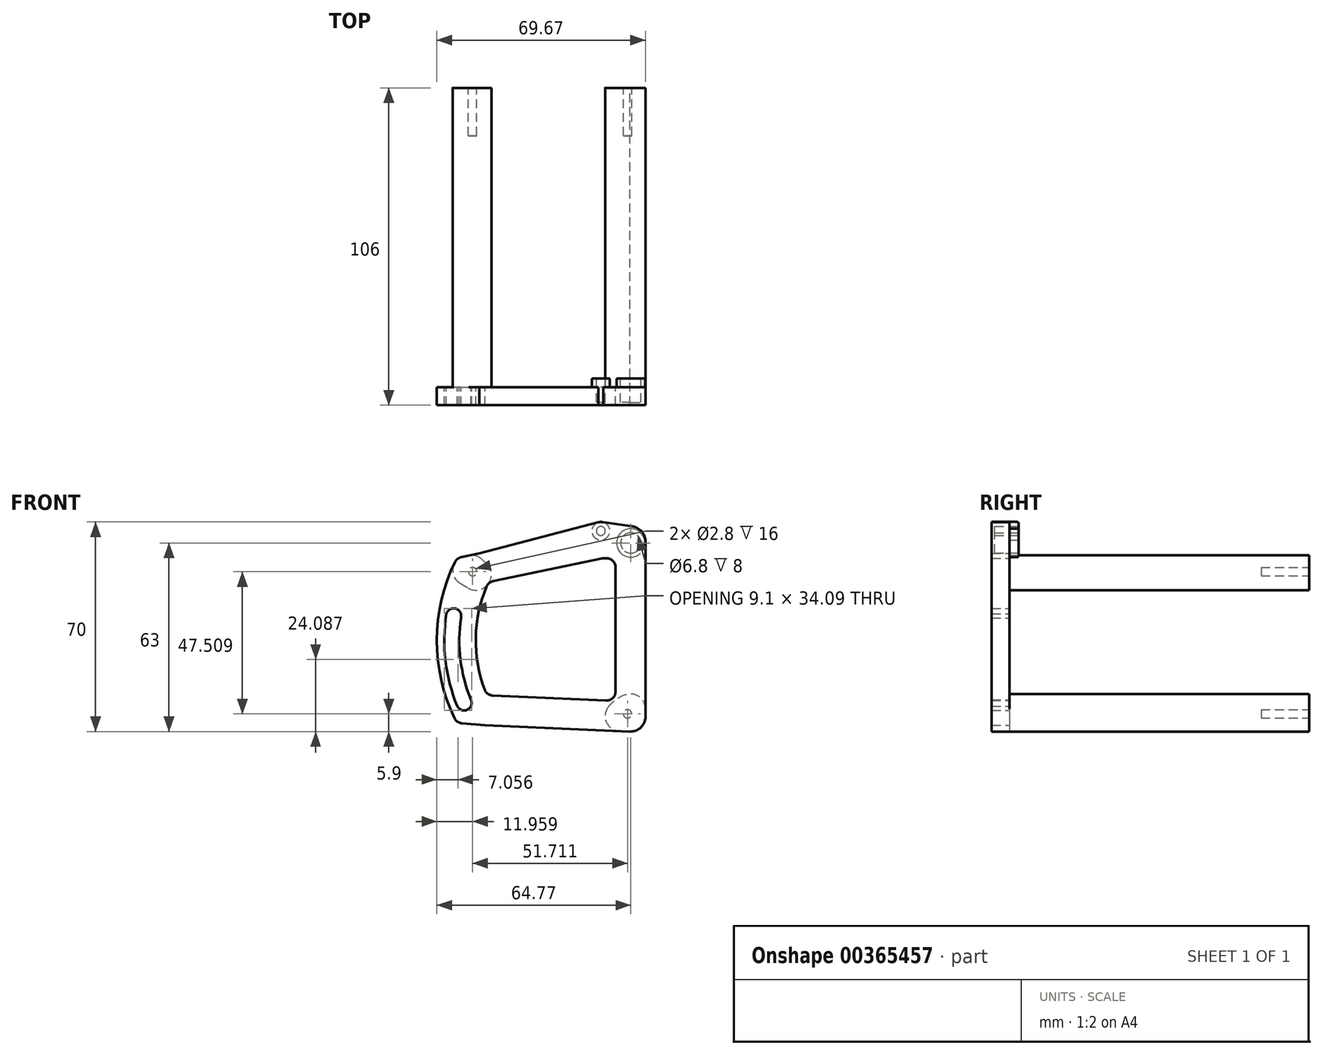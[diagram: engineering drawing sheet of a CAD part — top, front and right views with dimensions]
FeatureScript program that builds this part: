
annotation { "Feature Type Name" : "Feature", "Feature Type Description" : "" }
export const myFeature = defineFeature(function(context is Context, id is Id, definition is map)
    precondition{}
    {
        {
            var Q0;
            Q0=qCreatedBy(makeId("Front.planeOp"),FACE);
            var sketch = newSketch(context, id + "F0", { "sketchPlane" : qUnion([Q0])});
            skLineSegment(sketch, "E0", {"start": v(0, 0) * mm, "end": v(0, 70) * mm});
            skLineSegment(sketch, "E1", {"start": v(-63, 5) * mm, "end": v(0, 0) * mm});
            skLineSegment(sketch, "E2", {"start": v(-63, 60) * mm, "end": v(-39, 65) * mm});
            skArc(sketch, "E3", {"start": v(-63, 60) * mm, "mid": v(-69.67, 32.5) * mm, "end": v(-63, 5) * mm});
            skLineSegment(sketch, "E4.0", {"start": v(-10, 60) * mm, "end": v(-13.97, 60) * mm});
            skLineSegment(sketch, "E4.1", {"start": v(-52.44, 51.98) * mm, "end": v(-13.97, 60) * mm});
            skLineSegment(sketch, "E4.2", {"start": v(-10, 12.33) * mm, "end": v(-10, 60) * mm});
            skCircle(sketch, "E5", {"center": v(-4.9, 65.1) * mm, "radius": 3.4 * mm});
            skPoint(sketch, "E6.endSnap0", {"position": v(-59.67, 32.9) * mm});
            skArc(sketch, "E7.0", {"start": v(-52.44, 51.98) * mm, "mid": v(-56.67, 33.17) * mm, "end": v(-52.98, 14.24) * mm});
            skArc(sketch, "E8.0.left", {"start": v(-61.63, 40.03) * mm, "mid": v(-61.79, 26.15) * mm, "end": v(-58.3, 12.71) * mm});
            skArc(sketch, "E8.0.right", {"start": v(-66.48, 41.42) * mm, "mid": v(-66.78, 25.74) * mm, "end": v(-62.83, 10.57) * mm});
            skArc(sketch, "E9", {"start": v(-62.83, 10.57) * mm, "mid": v(-59.5, 9.38) * mm, "end": v(-58.3, 12.71) * mm});
            skPoint(sketch, "E10.endSnap0", {"position": v(-67.17, 32.96) * mm});
            skArc(sketch, "E11", {"start": v(-61.63, 40.03) * mm, "mid": v(-63.36, 43.15) * mm, "end": v(-66.48, 41.42) * mm});
            skPoint(sketch, "E10.end.orphan", {"position": v(-67.17, 32.92) * mm});
            skLineSegment(sketch, "E12", {"start": v(-4.9, 65.1) * mm, "end": v(-14.9, 65.1) * mm});
            skLineSegment(sketch, "E13", {"start": v(-14.9, 65.1) * mm, "end": v(-14.9, 69.1) * mm});
            skCircle(sketch, "E14", {"center": v(-14.9, 69.1) * mm, "radius": 1.5 * mm});
            skArc(sketch, "E15", {"start": v(-14.06, 71.98) * mm, "mid": v(-14.91, 72.1) * mm, "end": v(-15.76, 71.97) * mm});
            skLineSegment(sketch, "E16", {"start": v(0, 70) * mm, "end": v(-14.06, 71.98) * mm});
            skLineSegment(sketch, "E17", {"start": v(-39, 65) * mm, "end": v(-15.76, 71.97) * mm});
            skLineSegment(sketch, "E18", {"start": v(-4.9, 65.1) * mm, "end": v(5.1, 65.1) * mm});
            skLineSegment(sketch, "E19", {"start": v(5.1, 65.1) * mm, "end": v(5.1, 75.1) * mm});
            skLineSegment(sketch, "E20", {"start": v(5.1, 75.1) * mm, "end": v(5.1, 2.1) * mm});
            skLineSegment(sketch, "E21", {"start": v(-10, 12.33) * mm, "end": v(-52.98, 14.24) * mm});
            skSolve(sketch);
        }
        {
            var Q0;
            Q0 = qSketchRegion(id + "F0", true);
            extrude(context, id + "F1", {"entities" : qUnion([Q0]), "depth" : 6 * mm});
        }
        {
            var Q0;
            Q0=makeQuery(id+"F1.opExtrude","SWEPT_EDGE",EDGE,{"disambiguationData":[OSD([sQuery(id+"F0.wireOp",EDGE,"E1"),sQuery(id+"F0.wireOp",EDGE,"E3")])]});
            var Q1;
            Q1=makeQuery(id+"F1.opExtrude","SWEPT_EDGE",EDGE,{"disambiguationData":[OSD([sQuery(id+"F0.wireOp",EDGE,"E2"),sQuery(id+"F0.wireOp",EDGE,"E3")])]});
            var Q2;
            Q2=makeQuery(id+"F1.opExtrude","SWEPT_EDGE",EDGE,{"disambiguationData":[OSD([sQuery(id+"F0.wireOp",EDGE,"kmYFCEJS-3rxs-r7UX-FBYq-gBhfxVAc6up7"),sQuery(id+"F0.wireOp",EDGE,"E2")])]});
            var Q3;
            Q3=makeQuery(id+"F1.opExtrude","SWEPT_EDGE",EDGE,{"disambiguationData":[OSD([sQuery(id+"F0.wireOp",EDGE,"E4.3"),sQuery(id+"F0.wireOp",EDGE,"E7.0")])]});
            var Q4;
            Q4=makeQuery(id+"F1.opExtrude","SWEPT_EDGE",EDGE,{"disambiguationData":[OSD([sQuery(id+"F0.wireOp",EDGE,"E4.1"),sQuery(id+"F0.wireOp",EDGE,"E7.0")])]});
            var Q5;
            Q5=makeQuery(id+"F1.opExtrude","SWEPT_EDGE",EDGE,{"disambiguationData":[OSD([sQuery(id+"F0.wireOp",EDGE,"E4.0"),sQuery(id+"F0.wireOp",EDGE,"E4.2")])]});
            var Q6;
            Q6=makeQuery(id+"F1.opExtrude","SWEPT_EDGE",EDGE,{"disambiguationData":[OSD([sQuery(id+"F0.wireOp",EDGE,"E4.0"),sQuery(id+"F0.wireOp",EDGE,"E4.1")])]});
            var Q7;
            Q7=makeQuery(id+"F1.opExtrude","SWEPT_EDGE",EDGE,{"disambiguationData":[OSD([sQuery(id+"F0.wireOp",EDGE,"E4.2"),sQuery(id+"F0.wireOp",EDGE,"E4.3")])]});
            fillet(context, id + "F2", {"entities" : qUnion([Q0, Q1, Q2, Q3, Q4, Q5, Q6, Q7]), "radius" : 3 * mm, "tangentPropagation" : true, "allowEdgeOverflow" : false});
        }
        {
            var Q0;
            Q0=makeQuery(id+"F1.opExtrude","CAP_FACE",FACE,{"disambiguationData":[OSD([sQuery(id+"F0.wireOp",EDGE,"E0"),sQuery(id+"F0.wireOp",EDGE,"kmYFCEJS-3rxs-r7UX-FBYq-gBhfxVAc6up7"),sQuery(id+"F0.wireOp",EDGE,"E1"),sQuery(id+"F0.wireOp",EDGE,"E2"),sQuery(id+"F0.wireOp",EDGE,"E3"),sQuery(id+"F0.wireOp",EDGE,"E4.0"),sQuery(id+"F0.wireOp",EDGE,"E4.1"),sQuery(id+"F0.wireOp",EDGE,"E4.2"),sQuery(id+"F0.wireOp",EDGE,"E4.3"),sQuery(id+"F0.wireOp",EDGE,"E5"),sQuery(id+"F0.wireOp",EDGE,"jneuIOKs-55e1-7TO2-QkRI-z34TiCrGb9SQ"),sQuery(id+"F0.wireOp",EDGE,"E7.0"),sQuery(id+"F0.wireOp",EDGE,"E8.0.left"),sQuery(id+"F0.wireOp",EDGE,"E8.0.right"),sQuery(id+"F0.wireOp",EDGE,"775hFTDc-WrRt-JcbV-c3o9-qAtFPoJClycm"),sQuery(id+"F0.wireOp",EDGE,"E9")])],"isStart":true});
            var sketch = newSketch(context, id + "F3", { "sketchPlane" : qUnion([Q0])});
            skLineSegment(sketch, "E22", {"start": v(3.24, 0.26) * mm, "end": v(14.95, 1.19) * mm});
            skLineSegment(sketch, "E23", {"start": v(0, 3.25) * mm, "end": v(0, 15) * mm});
            skLineSegment(sketch, "E24", {"start": v(0, 15) * mm, "end": v(10, 15) * mm});
            skLineSegment(sketch, "E25", {"start": v(14.95, 1.19) * mm, "end": v(14.95, 11.22) * mm});
            skLineSegment(sketch, "E26.0", {"start": v(-0.8, 9.97) * mm, "end": v(0, 10.03) * mm});
            skLineSegment(sketch, "E27.0", {"start": v(10, 0) * mm, "end": v(10, 0.8) * mm});
            skLineSegment(sketch, "E28", {"start": v(14.16, 11.16) * mm, "end": v(14.95, 11.22) * mm});
            skLineSegment(sketch, "E29.trimOffspring", {"start": v(10, 14.07) * mm, "end": v(10, 15) * mm});
            skLineSegment(sketch, "E30.trimOffspring", {"start": v(13.24, 11.08) * mm, "end": v(14.16, 11.16) * mm});
            skPoint(sketch, "E31.visualSharp", {"position": v(0, 0) * mm});
            skArc(sketch, "E31.filletArc", {"start": v(0, 3.25) * mm, "mid": v(0.96, 1.04) * mm, "end": v(3.24, 0.26) * mm});
            skPoint(sketch, "E32.visualSharp", {"position": v(10, 10.83) * mm});
            skArc(sketch, "E32.filletArc", {"start": v(10, 14.07) * mm, "mid": v(10.96, 11.87) * mm, "end": v(13.24, 11.08) * mm});
            skArc(sketch, "E33", {"start": v(65.72, 53.91) * mm, "mid": v(64.75, 56.31) * mm, "end": v(63.67, 58.67) * mm});
            skArc(sketch, "E34.0", {"start": v(54.33, 47.14) * mm, "mid": v(53.74, 48.84) * mm, "end": v(53.08, 50.51) * mm});
            skLineSegment(sketch, "E35", {"start": v(47.41, 53.03) * mm, "end": v(50.93, 52.3) * mm});
            skLineSegment(sketch, "E36", {"start": v(56.52, 61.35) * mm, "end": v(61.58, 60.3) * mm});
            skArc(sketch, "E37", {"start": v(63.67, 58.67) * mm, "mid": v(62.81, 59.72) * mm, "end": v(61.58, 60.3) * mm});
            skArc(sketch, "E38", {"start": v(53.08, 50.51) * mm, "mid": v(52.23, 51.67) * mm, "end": v(50.93, 52.3) * mm});
            skPoint(sketch, "E39.center.orphan", {"position": v(62.81, 59.72) * mm});
            skPoint(sketch, "E40.center.orphan", {"position": v(52.23, 51.67) * mm});
            skLineSegment(sketch, "E41", {"start": v(65.72, 53.91) * mm, "end": v(54.33, 47.14) * mm});
            skLineSegment(sketch, "E42", {"start": v(56.52, 61.35) * mm, "end": v(47.41, 53.03) * mm});
            skSolve(sketch);
        }
        {
            var Q0;
            Q0 = qSketchRegion(id + "F3", true);
            extrude(context, id + "F4", {"entities" : qUnion([Q0]), "operationType" : NewBodyOperationType.ADD, "depth" : 100 * mm});
        }
        {
            var Q0;
            Q0=makeQuery(id+"F4.opExtrude","SWEPT_EDGE",EDGE,{"disambiguationData":[OSD([sQuery(id+"F0.wireOp",EDGE,"E4.3"),sQuery(id+"F3.wireOp",EDGE,"E25"),sQuery(id+"F3.wireOp",EDGE,"E28")])]});
            var Q1;
            Q1=makeQuery(id+"F4.opExtrude","SWEPT_EDGE",EDGE,{"disambiguationData":[OSD([sQuery(id+"F0.wireOp",EDGE,"E4.2"),sQuery(id+"F3.wireOp",EDGE,"E24"),sQuery(id+"F3.wireOp",EDGE,"E29.trimOffspring")])]});
            fillet(context, id + "F5", {"entities" : qUnion([Q0, Q1]), "radius" : 12 * mm, "tangentPropagation" : true, "allowEdgeOverflow" : false});
        }
        {
            var Q0;
            Q0=makeQuery(id+"F4.opExtrude","SWEPT_EDGE",EDGE,{"disambiguationData":[OSD([sQuery(id+"F0.wireOp",EDGE,"E0"),sQuery(id+"F3.wireOp",EDGE,"E23"),sQuery(id+"F3.wireOp",EDGE,"E24")])]});
            var Q1;
            Q1=makeQuery(id+"F4.opExtrude","SWEPT_EDGE",EDGE,{"disambiguationData":[OSD([sQuery(id+"F0.wireOp",EDGE,"E1"),sQuery(id+"F3.wireOp",EDGE,"E22"),sQuery(id+"F3.wireOp",EDGE,"E25")])]});
            fillet(context, id + "F6", {"entities" : qUnion([Q0, Q1]), "radius" : 5 * mm, "tangentPropagation" : true, "allowEdgeOverflow" : false});
        }
        {
            var Q0;
            Q0=makeQuery(id+"F4.opExtrude","SWEPT_EDGE",EDGE,{"disambiguationData":[OSD([sQuery(id+"F0.wireOp",EDGE,"E7.0"),sQuery(id+"F3.wireOp",EDGE,"E34.0"),sQuery(id+"F3.wireOp",EDGE,"E41")])]});
            var Q1;
            Q1=makeQuery(id+"F4.opExtrude","SWEPT_EDGE",EDGE,{"disambiguationData":[OSD([sQuery(id+"F0.wireOp",EDGE,"E4.1"),sQuery(id+"F3.wireOp",EDGE,"E35"),sQuery(id+"F3.wireOp",EDGE,"E42")])]});
            var Q2;
            Q2=makeQuery(id+"F4.opExtrude","SWEPT_EDGE",EDGE,{"disambiguationData":[OSD([sQuery(id+"F0.wireOp",EDGE,"E2"),sQuery(id+"F3.wireOp",EDGE,"E36"),sQuery(id+"F3.wireOp",EDGE,"E42")])]});
            var Q3;
            Q3=makeQuery(id+"F4.opExtrude","SWEPT_EDGE",EDGE,{"disambiguationData":[OSD([sQuery(id+"F0.wireOp",EDGE,"E3"),sQuery(id+"F3.wireOp",EDGE,"E33"),sQuery(id+"F3.wireOp",EDGE,"E41")])]});
            fillet(context, id + "F7", {"entities" : qUnion([Q0, Q1, Q2, Q3]), "radius" : 5 * mm, "tangentPropagation" : true, "allowEdgeOverflow" : false});
        }
        {
            var Q0;
            {var subQ0=sQuery(id+"F0.wireOp",EDGE,"E2");var subQ1=sQuery(id+"F0.wireOp",EDGE,"kmYFCEJS-3rxs-r7UX-FBYq-gBhfxVAc6up7");var subQ2=sQuery(id+"F0.wireOp",EDGE,"E5");var subQ3=sQuery(id+"F0.wireOp",EDGE,"jneuIOKs-55e1-7TO2-QkRI-z34TiCrGb9SQ");var subQ4=sQuery(id+"F0.wireOp",EDGE,"E4.2");var subQ5=sQuery(id+"F0.wireOp",EDGE,"E4.1");var subQ6=sQuery(id+"F0.wireOp",EDGE,"E0");var subQ7=sQuery(id+"F0.wireOp",EDGE,"E4.0");Q0=makeQuery(id+"F4.boolean.opBoolean","SPLIT",FACE,{"disambiguationData":[TD([makeQuery(id+"F1.opExtrude","SWEPT_FACE",FACE,{"disambiguationData":[OSD([subQ6])]})])],"derivedFrom":makeQuery(id+"F1.opExtrude","CAP_FACE",FACE,{"disambiguationData":[OSD([subQ6,subQ1,sQuery(id+"F0.wireOp",EDGE,"E1"),subQ0,sQuery(id+"F0.wireOp",EDGE,"E3"),subQ7,subQ5,subQ4,sQuery(id+"F0.wireOp",EDGE,"E4.3"),subQ2,subQ3,sQuery(id+"F0.wireOp",EDGE,"E7.0"),sQuery(id+"F0.wireOp",EDGE,"E8.0.left"),sQuery(id+"F0.wireOp",EDGE,"E8.0.right"),sQuery(id+"F0.wireOp",EDGE,"E9"),sQuery(id+"F0.wireOp",EDGE,"E11")])],"isStart":true})});}
            var sketch = newSketch(context, id + "F8", { "sketchPlane" : qUnion([Q0])});
            skCircle(sketch, "E43", {"center": v(4.9, 65.1) * mm, "radius": 3.4 * mm});
            skCircle(sketch, "E44", {"center": v(4.9, 65.1) * mm, "radius": 4.75 * mm});
            skCircle(sketch, "E45", {"center": v(14.9, 69.1) * mm, "radius": 1.5 * mm});
            skCircle(sketch, "E46", {"center": v(14.9, 69.1) * mm, "radius": 3 * mm});
            skSolve(sketch);
        }
        {
            var Q0;
            Q0 = qSketchRegion(id + "F8", true);
            extrude(context, id + "F9", {"entities" : qUnion([Q0]), "operationType" : NewBodyOperationType.ADD, "depth" : 3 * mm});
        }
        {
            var Q0;
            Q0=makeQuery(id+"F1.opExtrude","CAP_FACE",FACE,{"disambiguationData":[OSD([sQuery(id+"F0.wireOp",EDGE,"E0"),sQuery(id+"F0.wireOp",EDGE,"kmYFCEJS-3rxs-r7UX-FBYq-gBhfxVAc6up7"),sQuery(id+"F0.wireOp",EDGE,"E1"),sQuery(id+"F0.wireOp",EDGE,"E2"),sQuery(id+"F0.wireOp",EDGE,"E3"),sQuery(id+"F0.wireOp",EDGE,"E4.0"),sQuery(id+"F0.wireOp",EDGE,"E4.1"),sQuery(id+"F0.wireOp",EDGE,"E4.2"),sQuery(id+"F0.wireOp",EDGE,"E4.3"),sQuery(id+"F0.wireOp",EDGE,"E5"),sQuery(id+"F0.wireOp",EDGE,"jneuIOKs-55e1-7TO2-QkRI-z34TiCrGb9SQ"),sQuery(id+"F0.wireOp",EDGE,"E7.0"),sQuery(id+"F0.wireOp",EDGE,"E8.0.left"),sQuery(id+"F0.wireOp",EDGE,"E8.0.right"),sQuery(id+"F0.wireOp",EDGE,"E9"),sQuery(id+"F0.wireOp",EDGE,"E11")])],"isStart":false});
            var sketch = newSketch(context, id + "F10", { "sketchPlane" : qUnion([Q0])});
            skCircle(sketch, "E47", {"center": v(-4.9, 65.1) * mm, "radius": 3.4 * mm});
            skCircle(sketch, "E48", {"center": v(-14.9, 69.1) * mm, "radius": 1.5 * mm});
            skSolve(sketch);
        }
        {
            var Q0;
            Q0 = qSketchRegion(id + "F10", true);
            extrude(context, id + "F11", {"entities" : qUnion([Q0]), "operationType" : NewBodyOperationType.ADD, "oppositeDirection" : true, "depth" : 1 * mm});
        }
        {
            var Q0;
            Q0=makeQuery(id+"F4.opExtrude","CAP_FACE",FACE,{"disambiguationData":[OSD([sQuery(id+"F3.wireOp",EDGE,"E33"),sQuery(id+"F3.wireOp",EDGE,"E34.0"),sQuery(id+"F3.wireOp",EDGE,"E35"),sQuery(id+"F3.wireOp",EDGE,"E36"),sQuery(id+"F3.wireOp",EDGE,"E37"),sQuery(id+"F3.wireOp",EDGE,"E38"),sQuery(id+"F3.wireOp",EDGE,"E41"),sQuery(id+"F3.wireOp",EDGE,"E42")])],"isStart":false});
            var sketch = newSketch(context, id + "F12", { "sketchPlane" : qUnion([Q0])});
            skCircle(sketch, "E49", {"center": v(57.71, 55.5) * mm, "radius": 1.4 * mm});
            skSolve(sketch);
        }
        {
            var Q0;
            Q0 = qSketchRegion(id + "F12", true);
            extrude(context, id + "F13", {"entities" : qUnion([Q0]), "operationType" : NewBodyOperationType.REMOVE, "oppositeDirection" : true, "depth" : 16 * mm});
        }
        {
            var Q0;
            Q0=makeQuery(id+"F4.opExtrude","CAP_FACE",FACE,{"disambiguationData":[OSD([sQuery(id+"F3.wireOp",EDGE,"E22"),sQuery(id+"F3.wireOp",EDGE,"E23"),sQuery(id+"F3.wireOp",EDGE,"E24"),sQuery(id+"F3.wireOp",EDGE,"E25"),sQuery(id+"F3.wireOp",EDGE,"E28"),sQuery(id+"F3.wireOp",EDGE,"E29.trimOffspring"),sQuery(id+"F3.wireOp",EDGE,"E30.trimOffspring"),sQuery(id+"F3.wireOp",EDGE,"E31.filletArc"),sQuery(id+"F3.wireOp",EDGE,"E32.filletArc")])],"isStart":false});
            var sketch = newSketch(context, id + "F14", { "sketchPlane" : qUnion([Q0])});
            skCircle(sketch, "E50", {"center": v(6, 8) * mm, "radius": 1.4 * mm});
            skSolve(sketch);
        }
        {
            var Q0;
            Q0 = qSketchRegion(id + "F14", true);
            extrude(context, id + "F15", {"entities" : qUnion([Q0]), "operationType" : NewBodyOperationType.REMOVE, "oppositeDirection" : true, "depth" : 16 * mm});
        }
        {
            var Q0;
            Q0=makeQuery(id+"F9.opExtrude","CAP_EDGE",EDGE,{"disambiguationData":[OSD([sQuery(id+"F8.wireOp",EDGE,"E44")])],"isStart":false});
            var Q1;
            Q1=makeQuery(id+"F9.opExtrude","CAP_EDGE",EDGE,{"disambiguationData":[OSD([sQuery(id+"F8.wireOp",EDGE,"E46")])],"isStart":false});
            fillet(context, id + "F16", {"entities" : qUnion([Q0, Q1]), "radius" : 0.5 * mm, "tangentPropagation" : true, "allowEdgeOverflow" : false});
        }
        {
            var Q0;
            Q0=makeQuery(id+"F1.opExtrude","SWEPT_EDGE",EDGE,{"disambiguationData":[OSD([sQuery(id+"F0.wireOp",EDGE,"E0"),sQuery(id+"F0.wireOp",EDGE,"E1")])]});
            fillet(context, id + "F17", {"entities" : qUnion([Q0]), "radius" : 6 * mm, "tangentPropagation" : true, "allowEdgeOverflow" : false});
        }
        {
            var Q0;
            Q0=makeQuery(id+"F1.opExtrude","SWEPT_EDGE",EDGE,{"disambiguationData":[OSD([sQuery(id+"F0.wireOp",EDGE,"E0"),sQuery(id+"F0.wireOp",EDGE,"E16")])]});
            fillet(context, id + "F18", {"entities" : qUnion([Q0]), "radius" : 5 * mm, "tangentPropagation" : true, "allowEdgeOverflow" : false});
        }
        {
            var Q0;
            Q0=makeQuery(id+"F4.opExtrude","CAP_FACE",FACE,{"disambiguationData":[OSD([sQuery(id+"F3.wireOp",EDGE,"E22"),sQuery(id+"F3.wireOp",EDGE,"E23"),sQuery(id+"F3.wireOp",EDGE,"E24"),sQuery(id+"F3.wireOp",EDGE,"E25"),sQuery(id+"F3.wireOp",EDGE,"E28"),sQuery(id+"F3.wireOp",EDGE,"E29.trimOffspring"),sQuery(id+"F3.wireOp",EDGE,"E30.trimOffspring"),sQuery(id+"F3.wireOp",EDGE,"E31.filletArc"),sQuery(id+"F3.wireOp",EDGE,"E32.filletArc")])],"isStart":false});
            var sketch = newSketch(context, id + "F19", { "sketchPlane" : qUnion([Q0])});
            skLineSegment(sketch, "E51", {"start": v(0, 0) * mm, "end": v(0, 2.1) * mm});
            skLineSegment(sketch, "E52", {"start": v(0, 2.1) * mm, "end": v(52.6, 2.1) * mm});
            skLineSegment(sketch, "E53", {"start": v(52.6, 2.1) * mm, "end": v(52.6, 0) * mm});
            skLineSegment(sketch, "E54", {"start": v(52.6, 0) * mm, "end": v(0, 0) * mm});
            skSolve(sketch);
        }
        {
            var Q0;
            Q0 = qSketchRegion(id + "F19", true);
            extrude(context, id + "F20", {"entities" : qUnion([Q0]), "operationType" : NewBodyOperationType.REMOVE, "oppositeDirection" : true, "depth" : 111.9 * mm});
        }
        {
            var Q0;
            Q0=makeQuery(id+"F20.boolean.opBoolean","INTERSECT",EDGE,{"derivedFrom":[makeQuery(id+"F4.boolean.opBoolean","MERGE",FACE,{"derivedFrom":[makeQuery(id+"F1.opExtrude","SWEPT_FACE",FACE,{"disambiguationData":[OSD([sQuery(id+"F0.wireOp",EDGE,"E1")])]}),makeQuery(id+"F4.opExtrude","SWEPT_FACE",FACE,{"disambiguationData":[OSD([sQuery(id+"F3.wireOp",EDGE,"E22")])]})]}),makeQuery(id+"F20.opExtrude","SWEPT_FACE",FACE,{"disambiguationData":[OSD([sQuery(id+"F19.wireOp",EDGE,"E52")])]})]});
            fillet(context, id + "F21", {"entities" : qUnion([Q0]), "radius" : 11 * mm, "tangentPropagation" : true, "allowEdgeOverflow" : false});
        }
        {
            var Q0;
            Q0=makeQuery(id+"F20.boolean.opBoolean","INTERSECT",EDGE,{"derivedFrom":[makeQuery(id+"F6.opFillet","BLEND_FACE",FACE,{"disambiguationData":[OSD([sQuery(id+"F0.wireOp",EDGE,"E1"),sQuery(id+"F3.wireOp",EDGE,"E22"),sQuery(id+"F3.wireOp",EDGE,"E25")])]}),makeQuery(id+"F20.opExtrude","SWEPT_FACE",FACE,{"disambiguationData":[OSD([sQuery(id+"F19.wireOp",EDGE,"E52")])]})]});
            fillet(context, id + "F22", {"entities" : qUnion([Q0]), "radius" : 5 * mm, "tangentPropagation" : true, "allowEdgeOverflow" : false});
        }
        {
            var Q0;
            Q0=makeQuery(id+"F20.boolean.opBoolean","INTERSECT",EDGE,{"derivedFrom":[makeQuery(id+"F17.opFillet","BLEND_FACE",FACE,{"disambiguationData":[OSD([sQuery(id+"F0.wireOp",EDGE,"E0"),sQuery(id+"F0.wireOp",EDGE,"E1")])]}),makeQuery(id+"F20.opExtrude","SWEPT_FACE",FACE,{"disambiguationData":[OSD([sQuery(id+"F19.wireOp",EDGE,"E52")])]})]});
            fillet(context, id + "F23", {"entities" : qUnion([Q0]), "radius" : 5 * mm, "tangentPropagation" : true, "allowEdgeOverflow" : false});
        }
        {
            var Q0;
            {var subQ0=sQuery(id+"F0.wireOp",EDGE,"E21");var subQ1=sQuery(id+"F0.wireOp",EDGE,"E17");var subQ2=sQuery(id+"F0.wireOp",EDGE,"E16");var subQ3=sQuery(id+"F0.wireOp",EDGE,"E15");var subQ4=sQuery(id+"F0.wireOp",EDGE,"E14");var subQ5=sQuery(id+"F0.wireOp",EDGE,"E11");var subQ6=sQuery(id+"F0.wireOp",EDGE,"E4.1");var subQ7=sQuery(id+"F0.wireOp",EDGE,"E4.0");var subQ8=sQuery(id+"F0.wireOp",EDGE,"E9");var subQ9=sQuery(id+"F0.wireOp",EDGE,"E4.2");var subQ10=sQuery(id+"F0.wireOp",EDGE,"E8.0.right");var subQ11=sQuery(id+"F0.wireOp",EDGE,"E2");var subQ12=sQuery(id+"F0.wireOp",EDGE,"E1");var subQ13=sQuery(id+"F0.wireOp",EDGE,"E3");var subQ14=sQuery(id+"F0.wireOp",EDGE,"E0");var subQ15=sQuery(id+"F0.wireOp",EDGE,"E8.0.left");var subQ16=sQuery(id+"F0.wireOp",EDGE,"E5");var subQ17=sQuery(id+"F0.wireOp",EDGE,"E7.0");Q0=makeQuery(id+"F4.boolean.opBoolean","SPLIT",FACE,{"disambiguationData":[TD([makeQuery(id+"F1.opExtrude","SWEPT_FACE",FACE,{"disambiguationData":[OSD([subQ11])]})])],"derivedFrom":makeQuery(id+"F1.opExtrude","CAP_FACE",FACE,{"disambiguationData":[OSD([subQ14,subQ12,subQ11,subQ13,subQ7,subQ6,subQ9,subQ16,subQ17,subQ15,subQ10,subQ8,subQ5,subQ4,subQ3,subQ2,subQ1,subQ0])],"isStart":true})});}
            var sketch = newSketch(context, id + "F24", { "sketchPlane" : qUnion([Q0])});
            skLineSegment(sketch, "E55", {"start": v(13.13, 12.46) * mm, "end": v(51.04, 14.15) * mm});
            skLineSegment(sketch, "E56.0", {"start": v(13.58, 2.47) * mm, "end": v(51.49, 4.16) * mm});
            skLineSegment(sketch, "E57", {"start": v(51.49, 4.16) * mm, "end": v(61.48, 4.6) * mm});
            skLineSegment(sketch, "E58", {"start": v(13.58, 2.47) * mm, "end": v(3.59, 2.03) * mm});
            skLineSegment(sketch, "E59", {"start": v(3.59, 2.03) * mm, "end": v(3.65, 0.52) * mm});
            skLineSegment(sketch, "E60", {"start": v(3.65, 0.52) * mm, "end": v(61.82, 1.27) * mm});
            skLineSegment(sketch, "E61", {"start": v(61.82, 1.27) * mm, "end": v(61.48, 4.6) * mm});
            skSolve(sketch);
        }
        {
            var Q0;
            Q0 = qSketchRegion(id + "F24", true);
            extrude(context, id + "F25", {"entities" : qUnion([Q0]), "operationType" : NewBodyOperationType.REMOVE, "endBound" : BoundingType.SYMMETRIC, "oppositeDirection" : true, "depth" : 856 * mm});
        }
        {
            var Q0;
            Q0=makeQuery(id+"F25.boolean.opBoolean","INTERSECT",EDGE,{"derivedFrom":[makeQuery(id+"F22.opFillet","BLEND_FACE",FACE,{"disambiguationData":[OSD([sQuery(id+"F0.wireOp",EDGE,"E1"),sQuery(id+"F3.wireOp",EDGE,"E22"),sQuery(id+"F3.wireOp",EDGE,"E25"),sQuery(id+"F19.wireOp",EDGE,"E52")])]}),makeQuery(id+"F25.opExtrude","SWEPT_FACE",FACE,{"disambiguationData":[OSD([sQuery(id+"F24.wireOp",EDGE,"E56.0"),sQuery(id+"F24.wireOp",EDGE,"E57"),sQuery(id+"F24.wireOp",EDGE,"E58")])]})]});
            fillet(context, id + "F26", {"entities" : qUnion([Q0]), "radius" : 5 * mm, "tangentPropagation" : true, "allowEdgeOverflow" : false});
        }
        {
            var Q0;
            {var subQ0=sQuery(id+"F0.wireOp",EDGE,"E21");var subQ1=sQuery(id+"F0.wireOp",EDGE,"E17");var subQ2=sQuery(id+"F0.wireOp",EDGE,"E16");var subQ3=sQuery(id+"F0.wireOp",EDGE,"E15");var subQ4=sQuery(id+"F0.wireOp",EDGE,"E14");var subQ5=sQuery(id+"F0.wireOp",EDGE,"E11");var subQ6=sQuery(id+"F0.wireOp",EDGE,"E4.1");var subQ7=sQuery(id+"F0.wireOp",EDGE,"E4.0");var subQ8=sQuery(id+"F0.wireOp",EDGE,"E9");var subQ9=sQuery(id+"F0.wireOp",EDGE,"E4.2");var subQ10=sQuery(id+"F0.wireOp",EDGE,"E8.0.right");var subQ11=sQuery(id+"F0.wireOp",EDGE,"E2");var subQ12=sQuery(id+"F0.wireOp",EDGE,"E1");var subQ13=sQuery(id+"F0.wireOp",EDGE,"E3");var subQ14=sQuery(id+"F0.wireOp",EDGE,"E0");var subQ15=sQuery(id+"F0.wireOp",EDGE,"E8.0.left");var subQ16=sQuery(id+"F0.wireOp",EDGE,"E5");var subQ17=sQuery(id+"F0.wireOp",EDGE,"E7.0");Q0=makeQuery(id+"F4.boolean.opBoolean","SPLIT",FACE,{"disambiguationData":[TD([makeQuery(id+"F1.opExtrude","SWEPT_FACE",FACE,{"disambiguationData":[OSD([subQ11])]})])],"derivedFrom":makeQuery(id+"F1.opExtrude","CAP_FACE",FACE,{"disambiguationData":[OSD([subQ14,subQ12,subQ11,subQ13,subQ7,subQ6,subQ9,subQ16,subQ17,subQ15,subQ10,subQ8,subQ5,subQ4,subQ3,subQ2,subQ1,subQ0])],"isStart":true})});}
            var sketch = newSketch(context, id + "F27", { "sketchPlane" : qUnion([Q0])});
            skLineSegment(sketch, "E62", {"start": v(15.76, 71.97) * mm, "end": v(55.44, 61.57) * mm});
            skLineSegment(sketch, "E63", {"start": v(55.44, 61.57) * mm, "end": v(50.58, 60.14) * mm});
            skLineSegment(sketch, "E64", {"start": v(50.58, 60.14) * mm, "end": v(15.76, 71.97) * mm});
            skSolve(sketch);
        }
        {
            var Q0;
            Q0 = qSketchRegion(id + "F27", true);
            var Q1;
            Q1=makeQuery(id+"F11.boolean.opBoolean","MERGE",FACE,{"derivedFrom":[makeQuery(id+"F1.opExtrude","CAP_FACE",FACE,{"disambiguationData":[OSD([sQuery(id+"F0.wireOp",EDGE,"E0"),sQuery(id+"F0.wireOp",EDGE,"E1"),sQuery(id+"F0.wireOp",EDGE,"E2"),sQuery(id+"F0.wireOp",EDGE,"E3"),sQuery(id+"F0.wireOp",EDGE,"E4.0"),sQuery(id+"F0.wireOp",EDGE,"E4.1"),sQuery(id+"F0.wireOp",EDGE,"E4.2"),sQuery(id+"F0.wireOp",EDGE,"E5"),sQuery(id+"F0.wireOp",EDGE,"E7.0"),sQuery(id+"F0.wireOp",EDGE,"E8.0.left"),sQuery(id+"F0.wireOp",EDGE,"E8.0.right"),sQuery(id+"F0.wireOp",EDGE,"E9"),sQuery(id+"F0.wireOp",EDGE,"E11"),sQuery(id+"F0.wireOp",EDGE,"E14"),sQuery(id+"F0.wireOp",EDGE,"E15"),sQuery(id+"F0.wireOp",EDGE,"E16"),sQuery(id+"F0.wireOp",EDGE,"E17"),sQuery(id+"F0.wireOp",EDGE,"E21")])],"isStart":false}),makeQuery(id+"F11.opExtrude","CAP_FACE",FACE,{"disambiguationData":[OSD([sQuery(id+"F10.wireOp",EDGE,"E47")])],"isStart":true}),makeQuery(id+"F11.opExtrude","CAP_FACE",FACE,{"disambiguationData":[OSD([sQuery(id+"F10.wireOp",EDGE,"E48")])],"isStart":true})]});
            extrude(context, id + "F28", {"entities" : qUnion([Q0]), "operationType" : NewBodyOperationType.ADD, "endBound" : BoundingType.UP_TO_SURFACE, "oppositeDirection" : true, "endBoundEntityFace" : qUnion([Q1]), "depth" : 25 * mm});
        }
    });
